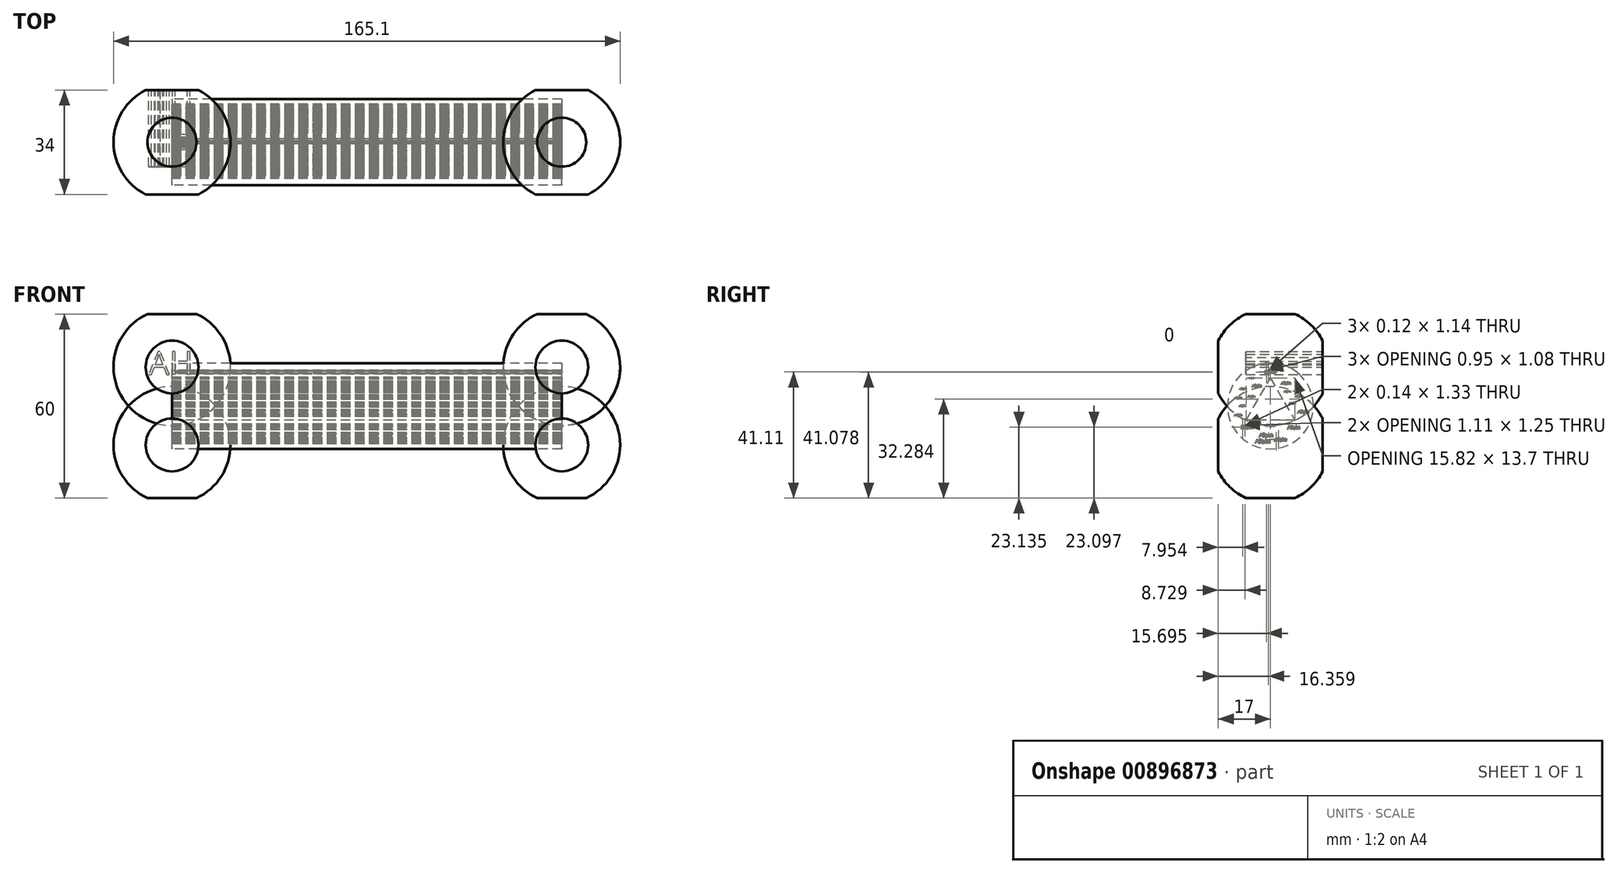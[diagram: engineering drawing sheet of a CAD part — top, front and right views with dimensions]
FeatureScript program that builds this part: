
annotation { "Feature Type Name" : "Feature", "Feature Type Description" : "" }
export const myFeature = defineFeature(function(context is Context, id is Id, definition is map)
    precondition{}
    {
        {
            var Q0;
            Q0=qCreatedBy(makeId("Front.planeOp"),FACE);
            var sketch = newSketch(context, id + "F0", { "sketchPlane" : qUnion([Q0])});
            skLineSegment(sketch, "E0.bottom", {"start": v(-63.5, 12.7) * mm, "end": v(63.5, 12.7) * mm, "construction": true});
            skLineSegment(sketch, "E0.top", {"start": v(-63.5, -12.7) * mm, "end": v(63.5, -12.7) * mm, "construction": true});
            skLineSegment(sketch, "E0.left", {"start": v(-63.5, 12.7) * mm, "end": v(-63.5, -12.7) * mm, "construction": true});
            skLineSegment(sketch, "E0.right", {"start": v(63.5, 12.7) * mm, "end": v(63.5, -12.7) * mm, "construction": true});
            skPoint(sketch, "E0.middle", {"position": v(0, 0) * mm});
            skArc(sketch, "E1", {"start": v(-44.45, 12.7) * mm, "mid": v(-63.5, 31.75) * mm, "end": v(-82.55, 12.7) * mm});
            skArc(sketch, "E2", {"start": v(-82.55, -12.7) * mm, "mid": v(-63.5, -31.75) * mm, "end": v(-44.45, -12.7) * mm});
            skArc(sketch, "E3", {"start": v(44.45, -12.7) * mm, "mid": v(63.5, -31.75) * mm, "end": v(82.55, -12.7) * mm});
            skArc(sketch, "E4", {"start": v(82.55, 12.7) * mm, "mid": v(63.5, 31.75) * mm, "end": v(44.45, 12.7) * mm});
            skLineSegment(sketch, "E5", {"start": v(-44.45, 12.7) * mm, "end": v(-82.55, 12.7) * mm});
            skLineSegment(sketch, "E6", {"start": v(-82.55, -12.7) * mm, "end": v(-44.45, -12.7) * mm});
            skLineSegment(sketch, "E7", {"start": v(44.45, -12.7) * mm, "end": v(82.55, -12.7) * mm});
            skLineSegment(sketch, "E8", {"start": v(44.45, 12.7) * mm, "end": v(82.55, 12.7) * mm});
            skSolve(sketch);
        }
        {
            var Q0;
            Q0=makeQuery(id+"F0.imprint","IMPRINT",FACE,{"disambiguationData":[TD([[makeQuery(id+"F0.imprint","IMPRINT",EDGE,{"derivedFrom":sQuery(id+"F0.wireOp",EDGE,"E1")}),1.0]])]});
            var Q1;
            Q1=makeQuery(id+"F0.imprint","IMPRINT",FACE,{"disambiguationData":[TD([[makeQuery(id+"F0.imprint","IMPRINT",EDGE,{"derivedFrom":sQuery(id+"F0.wireOp",EDGE,"E4")}),1.0]])]});
            var Q2;
            Q2=sQuery(id+"F0.wireOp",EDGE,"E0.bottom");
            revolve(context, id + "F1", {"surfaceOperationType" : NewSurfaceOperationType.NEW, "entities" : qUnion([Q0, Q1]), "axis" : qUnion([Q2]), "revolveType" : RevolveType.FULL});
        }
        {
            var Q0;
            Q0=makeQuery(id+"F0.imprint","IMPRINT",FACE,{"disambiguationData":[TD([[makeQuery(id+"F0.imprint","IMPRINT",EDGE,{"derivedFrom":sQuery(id+"F0.wireOp",EDGE,"E2")}),1.0]])]});
            var Q1;
            Q1=makeQuery(id+"F0.imprint","IMPRINT",FACE,{"disambiguationData":[TD([[makeQuery(id+"F0.imprint","IMPRINT",EDGE,{"derivedFrom":sQuery(id+"F0.wireOp",EDGE,"E3")}),1.0]])]});
            var Q2;
            Q2=sQuery(id+"F0.wireOp",EDGE,"E0.top");
            revolve(context, id + "F2", {"surfaceOperationType" : NewSurfaceOperationType.NEW, "entities" : qUnion([Q0, Q1]), "axis" : qUnion([Q2]), "revolveType" : RevolveType.FULL});
        }
        {
            var Q0;
            Q0=qCreatedBy(makeId("Right.planeOp"),FACE);
            var sketch = newSketch(context, id + "F3", { "sketchPlane" : qUnion([Q0])});
            skCircle(sketch, "E9", {"center": v(0, 0) * mm, "radius": 14 * mm});
            skCircle(sketch, "E10.cCircle", {"center": v(0, 0) * mm, "radius": 4.57 * mm, "construction": true});
            skLineSegment(sketch, "E10.0", {"start": v(7.91, -4.57) * mm, "end": v(-7.91, -4.57) * mm});
            skLineSegment(sketch, "E10.1", {"start": v(-7.91, -4.57) * mm, "end": v(0, 9.14) * mm});
            skLineSegment(sketch, "E10.2", {"start": v(0, 9.14) * mm, "end": v(7.91, -4.57) * mm});
            skPoint(sketch, "E10.0.midPoint", {"position": v(0, -4.57) * mm});
            skText(sketch, "E11", { "text": "Alain\n", "fontName": "OpenSans-Regular.ttf"});
            skText(sketch, "E12", { "text": "Alain\n", "fontName": "OpenSans-Regular.ttf"});
            skText(sketch, "E13", { "text": "Alain", "fontName": "OpenSans-Regular.ttf"});
            skText(sketch, "E14", { "text": "Alain\n", "fontName": "OpenSans-Regular.ttf"});
            skText(sketch, "E15", { "text": "Alain\n", "fontName": "OpenSans-Regular.ttf"});
            skText(sketch, "E16", { "text": "Alain\n", "fontName": "OpenSans-Regular.ttf"});
            skText(sketch, "E17", { "text": "Alain", "fontName": "OpenSans-Regular.ttf"});
            skText(sketch, "E18", { "text": "Alain", "fontName": "OpenSans-Regular.ttf"});
            skText(sketch, "E19", { "text": "Alain\n", "fontName": "OpenSans-Regular.ttf"});
            skText(sketch, "E20", { "text": "Alain\n", "fontName": "OpenSans-Regular.ttf"});
            skText(sketch, "E21", { "text": "Alain\n", "fontName": "OpenSans-Regular.ttf"});
            skText(sketch, "E22", { "text": "Alain\n", "fontName": "OpenSans-Regular.ttf"});
            skText(sketch, "E23", { "text": "Alain", "fontName": "OpenSans-Regular.ttf"});
            skText(sketch, "E24", { "text": "Alain\n", "fontName": "OpenSans-Regular.ttf"});
            skText(sketch, "E25", { "text": "Alain\n", "fontName": "OpenSans-Regular.ttf"});
            skText(sketch, "E26", { "text": "Alain\n", "fontName": "OpenSans-Regular.ttf"});
            skText(sketch, "E27", { "text": "Alain\n", "fontName": "OpenSans-Regular.ttf"});
            skText(sketch, "E28", { "text": "Alain\n", "fontName": "OpenSans-Regular.ttf"});
            skText(sketch, "E29", { "text": "Alain", "fontName": "OpenSans-Regular.ttf"});
            const initialGuessF3  = {"E11": [0.00612, 0.00058, 1, 0, 0.00063], "E12": [-0.0101, 0.00528, 1, 0, 0.0007], "E13": [-0.01179, 0.0023, 1, 0, 0.00078], "E14": [-0.00704, 0.00887, 1, 0, 0.00053], "E15": [-0.01015, -0.00022, 1, 0, 0.00064], "E16": [-0.0074, 0.00275, 1, 0, 0.00074], "E17": [-0.00602, 0.00613, 1, 0, 0.001], "E18": [-0.01182, -0.00335, 1, 0, 0.00081], "E19": [0.00345, 0.00702, 1, 0, 0.00102], "E20": [0.0044, 0.00438, 1, 0, 0.0007], "E21": [0.00806, 0.00282, 1, 0, 0.00077], "E22": [-0.00178, 0.01054, 1, 0, 0.00108], "E23": [0.00889, -0.0024, 1, 0, 0.00115], "E24": [-0.0096, -0.00753, 1, 0, 0.00126], "E25": [-0.00133, -0.00676, 1, 0, 0.00087], "E26": [0.00556, -0.00758, 1, 0, 0.00129], "E27": [-0.0037, -0.01018, 1, 0, 0.00143], "E28": [0.0013, -0.01154, 1, 0, 0.00126], "E29": [-0.005, -0.01222, 1, 0, 0.00157]};
            skSetInitialGuess(sketch, initialGuessF3);
            skSolve(sketch);
        }
        {
            var Q0;
            Q0=makeQuery(id+"F3.imprint","IMPRINT",FACE,{"disambiguationData":[TD([[makeQuery(id+"F3.imprint","IMPRINT",EDGE,{"derivedFrom":sQuery(id+"F3.wireOp",EDGE,"E9")}),1.0]])]});
            var Q1;
            Q1=makeQuery(id+"F1.opRevolve","SWEPT_BODY",BODY,{"disambiguationData":[OSD([sQuery(id+"F0.wireOp",EDGE,"E4"),sQuery(id+"F0.wireOp",EDGE,"E8")])]});
            extrude(context, id + "F4", {"entities" : qUnion([Q0]), "endBound" : BoundingType.SYMMETRIC, "depth" : 127 * mm, "endBoundEntityBody" : qUnion([Q1]), "offsetDistance" : 25.4 * mm});
        }
        {
            var Q0;
            Q0=qCreatedBy(makeId("Right.planeOp"),FACE);
            var sketch = newSketch(context, id + "F5", { "sketchPlane" : qUnion([Q0])});
            skLineSegment(sketch, "E30.bottom", {"start": v(-17, 30) * mm, "end": v(17, 30) * mm});
            skLineSegment(sketch, "E30.top", {"start": v(-17, -30) * mm, "end": v(17, -30) * mm});
            skLineSegment(sketch, "E30.left", {"start": v(-17, 30) * mm, "end": v(-17, -30) * mm});
            skLineSegment(sketch, "E30.right", {"start": v(17, 30) * mm, "end": v(17, -30) * mm});
            skLineSegment(sketch, "E31.bottom", {"start": v(-27, 40) * mm, "end": v(27, 40) * mm});
            skLineSegment(sketch, "E31.top", {"start": v(-27, -40) * mm, "end": v(27, -40) * mm});
            skLineSegment(sketch, "E31.left", {"start": v(-27, 40) * mm, "end": v(-27, -40) * mm});
            skLineSegment(sketch, "E31.right", {"start": v(27, 40) * mm, "end": v(27, -40) * mm});
            skLineSegment(sketch, "E32", {"start": v(0, -30) * mm, "end": v(0, 30) * mm, "construction": true});
            skLineSegment(sketch, "E33", {"start": v(-17, 0) * mm, "end": v(17, 0) * mm, "construction": true});
            skLineSegment(sketch, "E34", {"start": v(-17, 0) * mm, "end": v(-27, 0) * mm, "construction": true});
            skLineSegment(sketch, "E35", {"start": v(0, 30) * mm, "end": v(0, 40) * mm, "construction": true});
            skLineSegment(sketch, "E36", {"start": v(17, 0) * mm, "end": v(27, 0) * mm, "construction": true});
            skLineSegment(sketch, "E37", {"start": v(0, -30) * mm, "end": v(0, -40) * mm, "construction": true});
            skSolve(sketch);
        }
        {
            var Q0;
            Q0=qSketchRegion(id+"F5",true);
            extrude(context, id + "F6", {"entities" : qUnion([Q0]), "operationType" : NewBodyOperationType.REMOVE, "endBound" : BoundingType.THROUGH_ALL, "oppositeDirection" : true, "depth" : 25 * mm, "offsetDistance" : 25 * mm, "hasSecondDirection" : true, "secondDirectionBound" : SecondDirectionBoundingType.THROUGH_ALL, "secondDirectionOppositeDirection" : false, "secondDirectionDepth" : 25 * mm});
        }
        {
            var Q0;
            Q0=makeQuery(id+"F6.boolean.opBoolean","COPY",FACE,{"disambiguationData":[TD([makeQuery(id+"F1.opRevolve","SWEPT_FACE",FACE,{"disambiguationData":[OSD([sQuery(id+"F0.wireOp",EDGE,"E1")])]})])],"derivedFrom":makeQuery(id+"F6.opExtrude","SWEPT_FACE",FACE,{"disambiguationData":[OSD([sQuery(id+"F5.wireOp",EDGE,"E30.right")])]})});
            var sketch = newSketch(context, id + "F7", { "sketchPlane" : qUnion([Q0])});
            skText(sketch, "E38", { "text": "HA", "fontName": "OpenSans-Regular.ttf"});
            const initialGuessF7  = {"E38": [0.0566, 0.01024, 1, 0, 0.0076]};
            skSetInitialGuess(sketch, initialGuessF7);
            skSolve(sketch);
        }
        {
            var Q0;
            Q0 = qSketchRegion(id + "F7", true);
            extrude(context, id + "F8", {"entities" : qUnion([Q0]), "operationType" : NewBodyOperationType.REMOVE, "oppositeDirection" : true, "depth" : 25 * mm, "offsetDistance" : 25 * mm});
        }
    });
